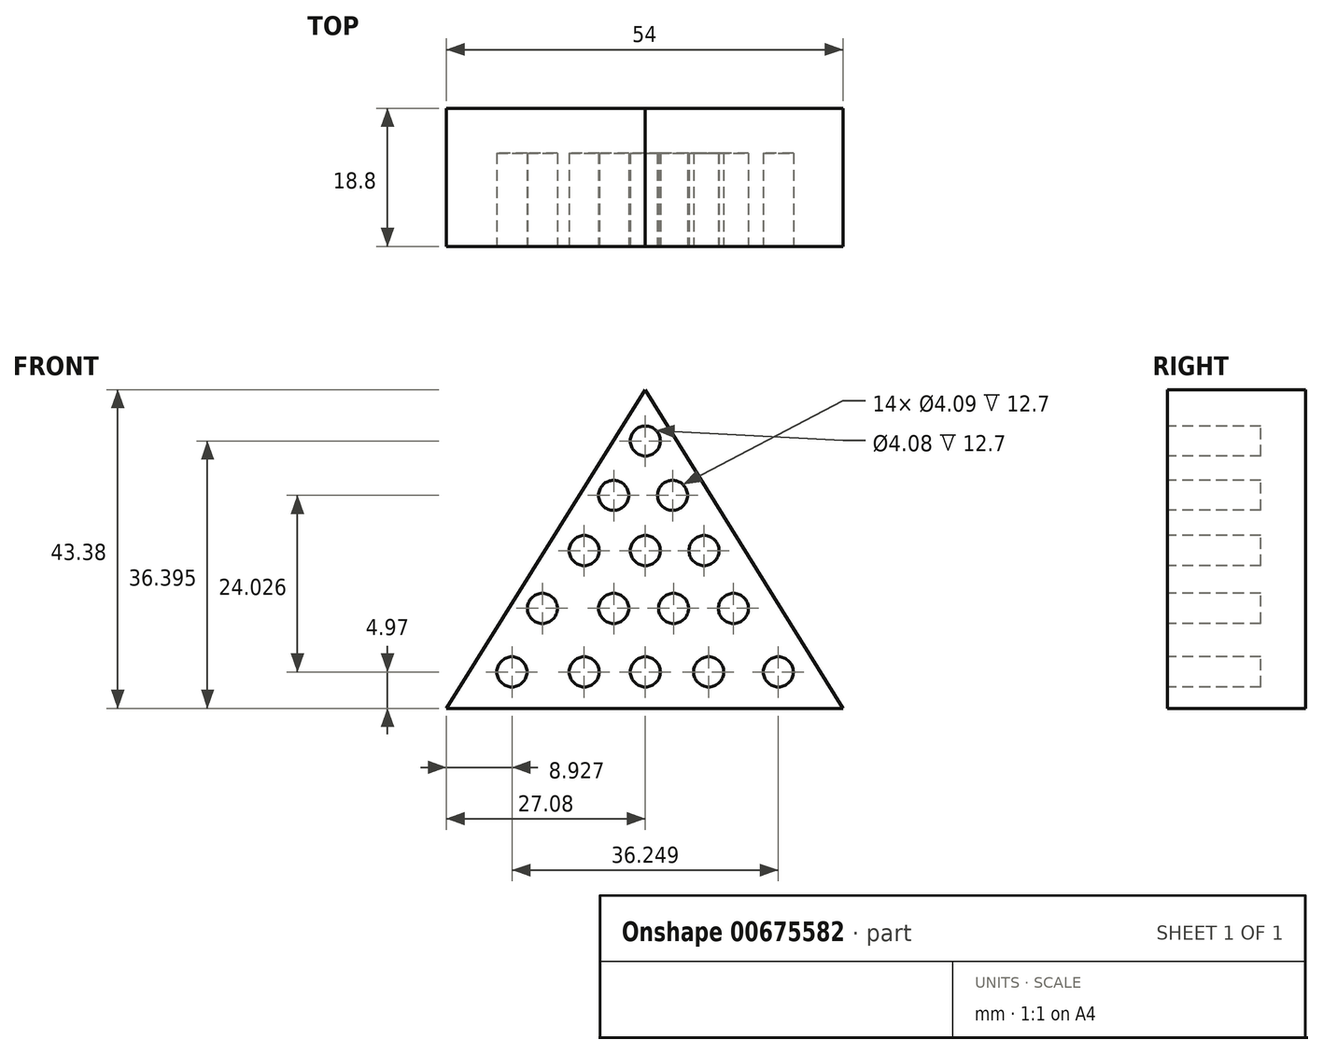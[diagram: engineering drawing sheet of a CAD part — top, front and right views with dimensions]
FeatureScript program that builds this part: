
annotation { "Feature Type Name" : "Feature", "Feature Type Description" : "" }
export const myFeature = defineFeature(function(context is Context, id is Id, definition is map)
    precondition{}
    {
        {
            var Q0;
            Q0=qCreatedBy(makeId("Front.planeOp"),FACE);
            var sketch = newSketch(context, id + "F0", { "sketchPlane" : qUnion([Q0])});
            skLineSegment(sketch, "E0", {"start": v(26.92, 12.28) * mm, "end": v(0, 55.66) * mm});
            skLineSegment(sketch, "E1", {"start": v(0, 55.66) * mm, "end": v(-27.08, 12.28) * mm});
            skLineSegment(sketch, "E2", {"start": v(-27.08, 12.28) * mm, "end": v(26.92, 12.28) * mm});
            skSolve(sketch);
        }
        {
            var Q0;
            Q0=makeQuery(id+"F0.imprint","IMPRINT",FACE,{"disambiguationData":[TD([[makeQuery(id+"F0.imprint","IMPRINT",EDGE,{"derivedFrom":sQuery(id+"F0.wireOp",EDGE,"QzceK57P-o3hb-tlJb-djLg-2mVzrRjcGdrI")}),1.0]])]});
            var Q1;
            Q1=makeQuery(id+"F0.imprint","IMPRINT",FACE,{"disambiguationData":[TD([[makeQuery(id+"F0.imprint","IMPRINT",EDGE,{"derivedFrom":sQuery(id+"F0.wireOp",EDGE,"E0")}),1.0]])]});
            extrude(context, id + "F1", {"entities" : qUnion([Q0, Q1]), "depth" : 1.02 * mm, "offsetDistance" : 25.4 * mm});
        }
        {
            var Q0;
            Q0=makeQuery(id+"F1.opExtrude","CAP_FACE",FACE,{"disambiguationData":[OSD([sQuery(id+"F0.wireOp",EDGE,"QzceK57P-o3hb-tlJb-djLg-2mVzrRjcGdrI"),sQuery(id+"F0.wireOp",EDGE,"E0"),sQuery(id+"F0.wireOp",EDGE,"E1")])],"isStart":false});
            extrude(context, id + "F2", {"entities" : qUnion([Q0]), "operationType" : NewBodyOperationType.ADD, "depth" : 17.78 * mm, "offsetDistance" : 25.4 * mm});
        }
        {
            var Q0;
            Q0=makeQuery(id+"F2.opExtrude","CAP_FACE",FACE,{"disambiguationData":[OSD([sQuery(id+"F0.wireOp",EDGE,"QzceK57P-o3hb-tlJb-djLg-2mVzrRjcGdrI"),sQuery(id+"F0.wireOp",EDGE,"E0"),sQuery(id+"F0.wireOp",EDGE,"E1")])],"isStart":false});
            var sketch = newSketch(context, id + "F3", { "sketchPlane" : qUnion([Q0])});
            skPoint(sketch, "E3.center.orphan", {"position": v(0, 48.67) * mm});
            skCircle(sketch, "E4", {"center": v(0, 48.67) * mm, "radius": 2.04 * mm});
            skCircle(sketch, "E5", {"center": v(-4.31, 41.28) * mm, "radius": 2.04 * mm});
            skCircle(sketch, "E6", {"center": v(3.7, 41.28) * mm, "radius": 2.04 * mm});
            skCircle(sketch, "E7", {"center": v(-8.32, 33.76) * mm, "radius": 2.04 * mm});
            skCircle(sketch, "E8", {"center": v(0, 33.76) * mm, "radius": 2.04 * mm});
            skCircle(sketch, "E9", {"center": v(7.98, 33.76) * mm, "radius": 2.04 * mm});
            skCircle(sketch, "E10", {"center": v(-14, 25.9) * mm, "radius": 2.04 * mm});
            skCircle(sketch, "E11", {"center": v(-4.31, 25.9) * mm, "radius": 2.04 * mm});
            skCircle(sketch, "E12", {"center": v(3.84, 25.9) * mm, "radius": 2.04 * mm});
            skCircle(sketch, "E13", {"center": v(11.98, 25.9) * mm, "radius": 2.04 * mm});
            skCircle(sketch, "E14", {"center": v(-18.15, 17.25) * mm, "radius": 2.04 * mm});
            skCircle(sketch, "E15", {"center": v(-8.32, 17.25) * mm, "radius": 2.04 * mm});
            skCircle(sketch, "E16", {"center": v(0, 17.25) * mm, "radius": 2.04 * mm});
            skCircle(sketch, "E17", {"center": v(8.61, 17.25) * mm, "radius": 2.04 * mm});
            skCircle(sketch, "E18", {"center": v(18.1, 17.25) * mm, "radius": 2.04 * mm});
            skSolve(sketch);
        }
        {
            var Q0;
            Q0=makeQuery(id+"F3.imprint","IMPRINT",FACE,{"disambiguationData":[TD([[makeQuery(id+"F3.imprint","IMPRINT",EDGE,{"derivedFrom":sQuery(id+"F3.wireOp",EDGE,"E6")}),1.0]])]});
            var Q1;
            Q1=makeQuery(id+"F3.imprint","IMPRINT",FACE,{"disambiguationData":[TD([[makeQuery(id+"F3.imprint","IMPRINT",EDGE,{"derivedFrom":sQuery(id+"F3.wireOp",EDGE,"E4")}),1.0]])]});
            var Q2;
            Q2=makeQuery(id+"F3.imprint","IMPRINT",FACE,{"disambiguationData":[TD([[makeQuery(id+"F3.imprint","IMPRINT",EDGE,{"derivedFrom":sQuery(id+"F3.wireOp",EDGE,"E5")}),1.0]])]});
            var Q3;
            Q3=makeQuery(id+"F3.imprint","IMPRINT",FACE,{"disambiguationData":[TD([[makeQuery(id+"F3.imprint","IMPRINT",EDGE,{"derivedFrom":sQuery(id+"F3.wireOp",EDGE,"E8")}),1.0]])]});
            var Q4;
            Q4=makeQuery(id+"F3.imprint","IMPRINT",FACE,{"disambiguationData":[TD([[makeQuery(id+"F3.imprint","IMPRINT",EDGE,{"derivedFrom":sQuery(id+"F3.wireOp",EDGE,"E9")}),1.0]])]});
            var Q5;
            Q5=makeQuery(id+"F3.imprint","IMPRINT",FACE,{"disambiguationData":[TD([[makeQuery(id+"F3.imprint","IMPRINT",EDGE,{"derivedFrom":sQuery(id+"F3.wireOp",EDGE,"E7")}),1.0]])]});
            var Q6;
            Q6=makeQuery(id+"F3.imprint","IMPRINT",FACE,{"disambiguationData":[TD([[makeQuery(id+"F3.imprint","IMPRINT",EDGE,{"derivedFrom":sQuery(id+"F3.wireOp",EDGE,"E11")}),1.0]])]});
            var Q7;
            Q7=makeQuery(id+"F3.imprint","IMPRINT",FACE,{"disambiguationData":[TD([[makeQuery(id+"F3.imprint","IMPRINT",EDGE,{"derivedFrom":sQuery(id+"F3.wireOp",EDGE,"E10")}),1.0]])]});
            var Q8;
            Q8=makeQuery(id+"F3.imprint","IMPRINT",FACE,{"disambiguationData":[TD([[makeQuery(id+"F3.imprint","IMPRINT",EDGE,{"derivedFrom":sQuery(id+"F3.wireOp",EDGE,"E12")}),1.0]])]});
            var Q9;
            Q9=makeQuery(id+"F3.imprint","IMPRINT",FACE,{"disambiguationData":[TD([[makeQuery(id+"F3.imprint","IMPRINT",EDGE,{"derivedFrom":sQuery(id+"F3.wireOp",EDGE,"E13")}),1.0]])]});
            var Q10;
            Q10=makeQuery(id+"F3.imprint","IMPRINT",FACE,{"disambiguationData":[TD([[makeQuery(id+"F3.imprint","IMPRINT",EDGE,{"derivedFrom":sQuery(id+"F3.wireOp",EDGE,"E18")}),1.0]])]});
            var Q11;
            Q11=makeQuery(id+"F3.imprint","IMPRINT",FACE,{"disambiguationData":[TD([[makeQuery(id+"F3.imprint","IMPRINT",EDGE,{"derivedFrom":sQuery(id+"F3.wireOp",EDGE,"E17")}),1.0]])]});
            var Q12;
            Q12=makeQuery(id+"F3.imprint","IMPRINT",FACE,{"disambiguationData":[TD([[makeQuery(id+"F3.imprint","IMPRINT",EDGE,{"derivedFrom":sQuery(id+"F3.wireOp",EDGE,"E16")}),1.0]])]});
            var Q13;
            Q13=makeQuery(id+"F3.imprint","IMPRINT",FACE,{"disambiguationData":[TD([[makeQuery(id+"F3.imprint","IMPRINT",EDGE,{"derivedFrom":sQuery(id+"F3.wireOp",EDGE,"E15")}),1.0]])]});
            var Q14;
            Q14=makeQuery(id+"F3.imprint","IMPRINT",FACE,{"disambiguationData":[TD([[makeQuery(id+"F3.imprint","IMPRINT",EDGE,{"derivedFrom":sQuery(id+"F3.wireOp",EDGE,"E14")}),1.0]])]});
            extrude(context, id + "F4", {"entities" : qUnion([Q0, Q1, Q2, Q3, Q4, Q5, Q6, Q7, Q8, Q9, Q10, Q11, Q12, Q13, Q14]), "operationType" : NewBodyOperationType.REMOVE, "oppositeDirection" : true, "depth" : 12.7 * mm, "offsetDistance" : 25.4 * mm});
        }
    });
